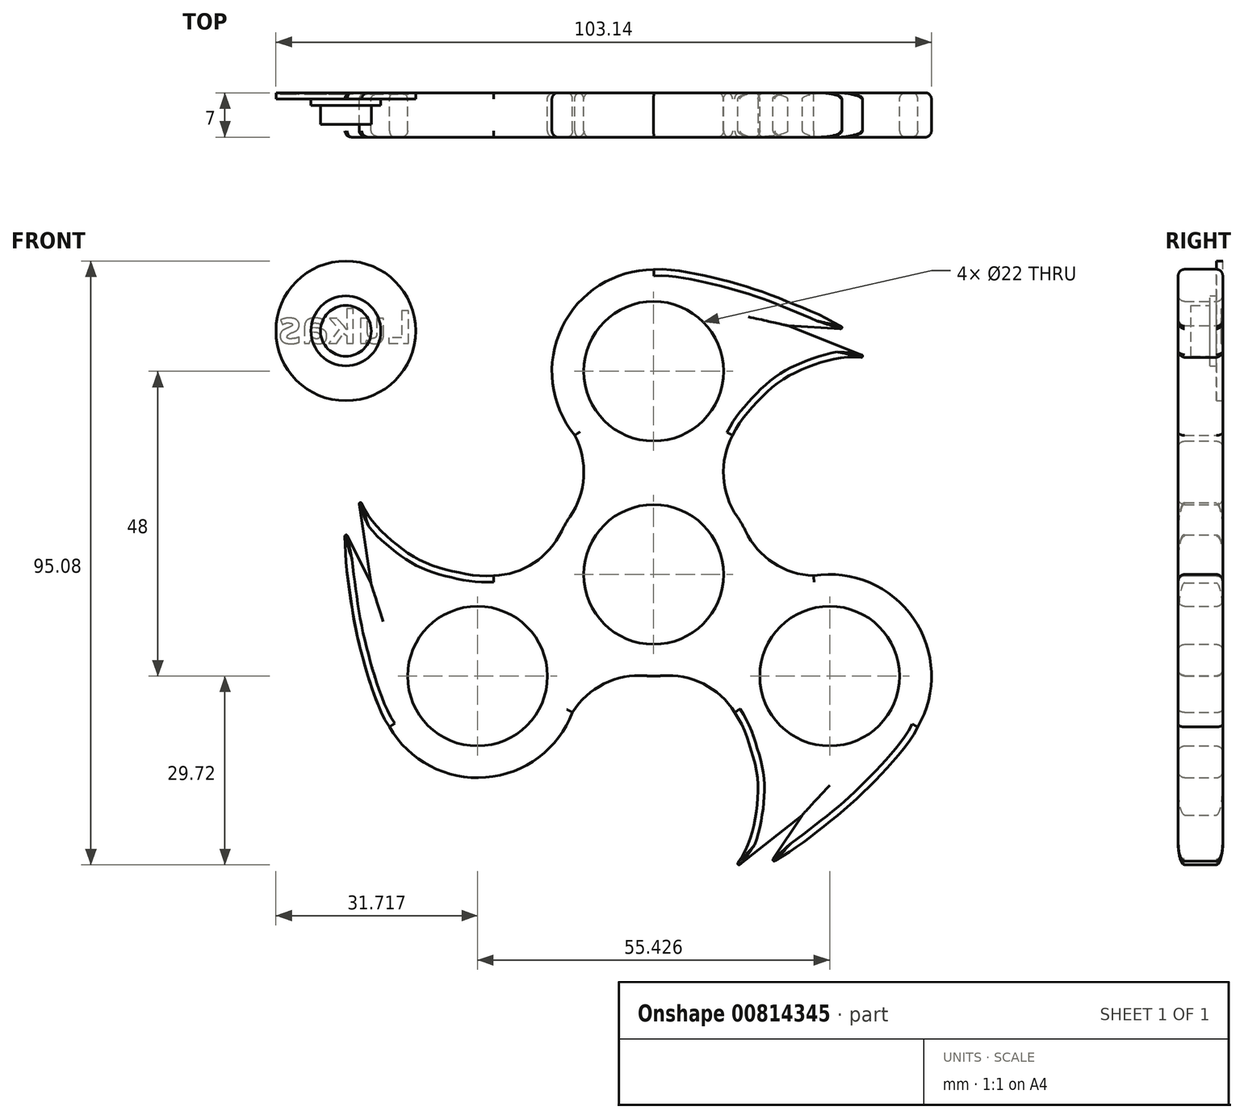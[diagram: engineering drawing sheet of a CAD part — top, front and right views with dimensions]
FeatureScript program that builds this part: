
annotation { "Feature Type Name" : "Feature", "Feature Type Description" : "" }
export const myFeature = defineFeature(function(context is Context, id is Id, definition is map)
    precondition{}
    {
        {
            var Q0;
            Q0=qCreatedBy(makeId("Front.planeOp"),FACE);
            var sketch = newSketch(context, id + "F0", { "sketchPlane" : qUnion([Q0])});
            skCircle(sketch, "E0", {"center": v(0, 0) * mm, "radius": 11 * mm});
            skArc(sketch, "E1", {"start": v(-13.17, 9.09) * mm, "mid": v(0, -16) * mm, "end": v(13.17, 9.09) * mm});
            skCircle(sketch, "E2", {"center": v(0, 32) * mm, "radius": 11 * mm});
            skLineSegment(sketch, "E3", {"start": v(12.42, 21.9) * mm, "end": v(12.42, 21.9) * mm});
            skFitSpline(sketch, "E4", {"points": [v(0, 48) * mm, v(15.63, 45) * mm, v(22.11, 42.54) * mm, v(30.28, 38.63) * mm], "startDerivative": vector(23.83, 2.95) * mm, "endDerivative": vector(45.32, -25.65) * mm});
            skLineSegment(sketch, "E5", {"start": v(30.28, 38.63) * mm, "end": v(21.1, 39.2) * mm});
            skLineSegment(sketch, "E6", {"start": v(21.1, 39.2) * mm, "end": v(34.96, 33.72) * mm});
            skFitSpline(sketch, "E7", {"points": [v(34.96, 33.72) * mm, v(23.56, 32.37) * mm, v(18.65, 29.47) * mm, v(15.85, 26.67) * mm, v(12.42, 21.9) * mm], "startDerivative": vector(-35.39, 11.82) * mm, "endDerivative": vector(-17.96, -33.28) * mm});
            skArc(sketch, "E8.trimOffspring", {"start": v(0, 48) * mm, "mid": v(-14.45, 38.88) * mm, "end": v(-12.42, 21.9) * mm});
            skArc(sketch, "E9", {"start": v(13.17, 9.09) * mm, "mid": v(11, 15.4) * mm, "end": v(12.42, 21.9) * mm});
            skArc(sketch, "E10.MirrorCS", {"start": v(-13.17, 9.09) * mm, "mid": v(-11, 15.4) * mm, "end": v(-12.42, 21.9) * mm});
            skSolve(sketch);
        }
        {
            var Q0;
            Q0=makeQuery(id+"F0.imprint","IMPRINT",FACE,{"disambiguationData":[TD([[makeQuery(id+"F0.imprint","IMPRINT",EDGE,{"derivedFrom":sQuery(id+"F0.wireOp",EDGE,"E0")}),-1.0]])]});
            extrude(context, id + "F1", {"entities" : qUnion([Q0]), "depth" : 7 * mm, "offsetDistance" : 25 * mm});
        }
        {
            var Q0;
            Q0=makeQuery(id+"F1.opExtrude","SWEPT_BODY",BODY,{"disambiguationData":[OSD([sQuery(id+"F0.wireOp",EDGE,"E0"),sQuery(id+"F0.wireOp",EDGE,"E1"),sQuery(id+"F0.wireOp",EDGE,"E2"),sQuery(id+"F0.wireOp",EDGE,"E3"),sQuery(id+"F0.wireOp",EDGE,"LkXJ2vyM-1mGQ-eDcK-5ijq-w6ZpazgIBIUJ"),sQuery(id+"F0.wireOp",EDGE,"5baaefb0-8613-44b4-96e0-c200b75026c80.MirrorCS"),sQuery(id+"F0.wireOp",EDGE,"E4"),sQuery(id+"F0.wireOp",EDGE,"E5"),sQuery(id+"F0.wireOp",EDGE,"E6"),sQuery(id+"F0.wireOp",EDGE,"E7"),sQuery(id+"F0.wireOp",EDGE,"E8.trimOffspring")])]});
            var Q1;
            Q1=makeQuery(id+"F1.opExtrude","SWEPT_FACE",FACE,{"disambiguationData":[OSD([sQuery(id+"F0.wireOp",EDGE,"E1")])]});
            circularPattern(context, id + "F2", {"entities" : qUnion([Q0]), "axis" : qUnion([Q1]), "angle" : 360 * degree, "instanceCount" : 3, "equalSpace" : true});
        }
        {
            var Q0;
            Q0=makeQuery(id+"F1.opExtrude","SWEPT_BODY",BODY,{"disambiguationData":[OSD([sQuery(id+"F0.wireOp",EDGE,"E0"),sQuery(id+"F0.wireOp",EDGE,"E1"),sQuery(id+"F0.wireOp",EDGE,"E2"),sQuery(id+"F0.wireOp",EDGE,"E3"),sQuery(id+"F0.wireOp",EDGE,"LkXJ2vyM-1mGQ-eDcK-5ijq-w6ZpazgIBIUJ"),sQuery(id+"F0.wireOp",EDGE,"5baaefb0-8613-44b4-96e0-c200b75026c80.MirrorCS"),sQuery(id+"F0.wireOp",EDGE,"E4"),sQuery(id+"F0.wireOp",EDGE,"E5"),sQuery(id+"F0.wireOp",EDGE,"E6"),sQuery(id+"F0.wireOp",EDGE,"E7"),sQuery(id+"F0.wireOp",EDGE,"E8.trimOffspring")])]});
            var Q1;
            Q1=makeQuery(id+"F2.opPattern","COPY",BODY,{"derivedFrom":makeQuery(id+"F1.opExtrude","SWEPT_BODY",BODY,{"disambiguationData":[OSD([sQuery(id+"F0.wireOp",EDGE,"E0"),sQuery(id+"F0.wireOp",EDGE,"E1"),sQuery(id+"F0.wireOp",EDGE,"E2"),sQuery(id+"F0.wireOp",EDGE,"E3"),sQuery(id+"F0.wireOp",EDGE,"LkXJ2vyM-1mGQ-eDcK-5ijq-w6ZpazgIBIUJ"),sQuery(id+"F0.wireOp",EDGE,"5baaefb0-8613-44b4-96e0-c200b75026c80.MirrorCS"),sQuery(id+"F0.wireOp",EDGE,"E4"),sQuery(id+"F0.wireOp",EDGE,"E5"),sQuery(id+"F0.wireOp",EDGE,"E6"),sQuery(id+"F0.wireOp",EDGE,"E7"),sQuery(id+"F0.wireOp",EDGE,"E8.trimOffspring")])]}),"instanceName":"1"});
            var Q2;
            Q2=makeQuery(id+"F2.opPattern","COPY",BODY,{"derivedFrom":makeQuery(id+"F1.opExtrude","SWEPT_BODY",BODY,{"disambiguationData":[OSD([sQuery(id+"F0.wireOp",EDGE,"E0"),sQuery(id+"F0.wireOp",EDGE,"E1"),sQuery(id+"F0.wireOp",EDGE,"E2"),sQuery(id+"F0.wireOp",EDGE,"E3"),sQuery(id+"F0.wireOp",EDGE,"LkXJ2vyM-1mGQ-eDcK-5ijq-w6ZpazgIBIUJ"),sQuery(id+"F0.wireOp",EDGE,"5baaefb0-8613-44b4-96e0-c200b75026c80.MirrorCS"),sQuery(id+"F0.wireOp",EDGE,"E4"),sQuery(id+"F0.wireOp",EDGE,"E5"),sQuery(id+"F0.wireOp",EDGE,"E6"),sQuery(id+"F0.wireOp",EDGE,"E7"),sQuery(id+"F0.wireOp",EDGE,"E8.trimOffspring")])]}),"instanceName":"2"});
            booleanBodies(context, id + "F3", {"operationType" : BooleanOperationType.UNION, "tools" : qUnion([Q0, Q1, Q2])});
        }
        {
            var Q0;
            {var subQ0=makeQuery(id+"F1.opExtrude","CAP_FACE",FACE,{"disambiguationData":[OSD([sQuery(id+"F0.wireOp",EDGE,"E0"),sQuery(id+"F0.wireOp",EDGE,"E1"),sQuery(id+"F0.wireOp",EDGE,"E2"),sQuery(id+"F0.wireOp",EDGE,"LkXJ2vyM-1mGQ-eDcK-5ijq-w6ZpazgIBIUJ"),sQuery(id+"F0.wireOp",EDGE,"5baaefb0-8613-44b4-96e0-c200b75026c80.MirrorCS"),sQuery(id+"F0.wireOp",EDGE,"E4"),sQuery(id+"F0.wireOp",EDGE,"E5"),sQuery(id+"F0.wireOp",EDGE,"E6"),sQuery(id+"F0.wireOp",EDGE,"E7"),sQuery(id+"F0.wireOp",EDGE,"E8.trimOffspring")])],"isStart":false});Q0=makeQuery(id+"F3.opBoolean","MERGE",FACE,{"derivedFrom":[subQ0,makeQuery(id+"F2.opPattern","COPY",FACE,{"derivedFrom":subQ0,"instanceName":"1"}),makeQuery(id+"F2.opPattern","COPY",FACE,{"derivedFrom":subQ0,"instanceName":"2"})]});}
            var Q1;
            {var subQ0=makeQuery(id+"F1.opExtrude","CAP_FACE",FACE,{"disambiguationData":[OSD([sQuery(id+"F0.wireOp",EDGE,"E0"),sQuery(id+"F0.wireOp",EDGE,"E1"),sQuery(id+"F0.wireOp",EDGE,"E2"),sQuery(id+"F0.wireOp",EDGE,"LkXJ2vyM-1mGQ-eDcK-5ijq-w6ZpazgIBIUJ"),sQuery(id+"F0.wireOp",EDGE,"5baaefb0-8613-44b4-96e0-c200b75026c80.MirrorCS"),sQuery(id+"F0.wireOp",EDGE,"E4"),sQuery(id+"F0.wireOp",EDGE,"E5"),sQuery(id+"F0.wireOp",EDGE,"E6"),sQuery(id+"F0.wireOp",EDGE,"E7"),sQuery(id+"F0.wireOp",EDGE,"E8.trimOffspring")])],"isStart":true});Q1=makeQuery(id+"F3.opBoolean","MERGE",FACE,{"derivedFrom":[subQ0,makeQuery(id+"F2.opPattern","COPY",FACE,{"derivedFrom":subQ0,"instanceName":"1"}),makeQuery(id+"F2.opPattern","COPY",FACE,{"derivedFrom":subQ0,"instanceName":"2"})]});}
            fillet(context, id + "F4", {"entities" : qUnion([Q0, Q1]), "radius" : 1 * mm, "tangentPropagation" : true, "allowEdgeOverflow" : false});
        }
        {
            var Q0;
            Q0=makeQuery(id+"F2.opPattern","COPY",EDGE,{"derivedFrom":makeQuery(id+"F1.opExtrude","SWEPT_EDGE",EDGE,{"disambiguationData":[OSD([sQuery(id+"F0.wireOp",EDGE,"E4"),sQuery(id+"F0.wireOp",EDGE,"E5")])]}),"instanceName":"2"});
            var Q1;
            Q1=makeQuery(id+"F2.opPattern","COPY",EDGE,{"derivedFrom":makeQuery(id+"F1.opExtrude","SWEPT_EDGE",EDGE,{"disambiguationData":[OSD([sQuery(id+"F0.wireOp",EDGE,"E6"),sQuery(id+"F0.wireOp",EDGE,"E7")])]}),"instanceName":"2"});
            var Q2;
            Q2=makeQuery(id+"F1.opExtrude","SWEPT_EDGE",EDGE,{"disambiguationData":[OSD([sQuery(id+"F0.wireOp",EDGE,"E6"),sQuery(id+"F0.wireOp",EDGE,"E7")])]});
            var Q3;
            Q3=makeQuery(id+"F1.opExtrude","SWEPT_EDGE",EDGE,{"disambiguationData":[OSD([sQuery(id+"F0.wireOp",EDGE,"E4"),sQuery(id+"F0.wireOp",EDGE,"E5")])]});
            var Q4;
            Q4=makeQuery(id+"F2.opPattern","COPY",EDGE,{"derivedFrom":makeQuery(id+"F1.opExtrude","SWEPT_EDGE",EDGE,{"disambiguationData":[OSD([sQuery(id+"F0.wireOp",EDGE,"E4"),sQuery(id+"F0.wireOp",EDGE,"E5")])]}),"instanceName":"1"});
            var Q5;
            Q5=makeQuery(id+"F2.opPattern","COPY",EDGE,{"derivedFrom":makeQuery(id+"F1.opExtrude","SWEPT_EDGE",EDGE,{"disambiguationData":[OSD([sQuery(id+"F0.wireOp",EDGE,"E6"),sQuery(id+"F0.wireOp",EDGE,"E7")])]}),"instanceName":"1"});
            fillet(context, id + "F5", {"entities" : qUnion([Q0, Q1, Q2, Q3, Q4, Q5]), "radius" : 0.2 * mm, "tangentPropagation" : true, "allowEdgeOverflow" : false});
        }
        {
            var Q0;
            Q0=qCreatedBy(makeId("Front.planeOp"),FACE);
            var sketch = newSketch(context, id + "F6", { "sketchPlane" : qUnion([Q0])});
            skCircle(sketch, "E11", {"center": v(-48.43, 38.36) * mm, "radius": 11 * mm});
            skCircle(sketch, "E12", {"center": v(-48.43, 38.36) * mm, "radius": 4 * mm});
            skCircle(sketch, "E13", {"center": v(-48.43, 38.36) * mm, "radius": 5.5 * mm});
            skSolve(sketch);
        }
        {
            var Q0;
            Q0=makeQuery(id+"F6.imprint","IMPRINT",FACE,{"disambiguationData":[TD([[makeQuery(id+"F6.imprint","IMPRINT",EDGE,{"derivedFrom":sQuery(id+"F6.wireOp",EDGE,"E11")}),1.0]])]});
            extrude(context, id + "F7", {"entities" : qUnion([Q0]), "depth" : 1 * mm, "offsetDistance" : 25 * mm});
        }
        {
            var Q0;
            Q0=makeQuery(id+"F6.imprint","IMPRINT",FACE,{"disambiguationData":[TD([[makeQuery(id+"F6.imprint","IMPRINT",EDGE,{"derivedFrom":sQuery(id+"F6.wireOp",EDGE,"E12")}),-1.0]])]});
            extrude(context, id + "F8", {"entities" : qUnion([Q0]), "operationType" : NewBodyOperationType.ADD, "depth" : 2 * mm, "offsetDistance" : 25 * mm});
        }
        {
            var Q0;
            Q0=makeQuery(id+"F6.imprint","IMPRINT",FACE,{"disambiguationData":[TD([[makeQuery(id+"F6.imprint","IMPRINT",EDGE,{"derivedFrom":sQuery(id+"F6.wireOp",EDGE,"E12")}),1.0]])]});
            extrude(context, id + "F9", {"entities" : qUnion([Q0]), "operationType" : NewBodyOperationType.ADD, "depth" : 5 * mm, "offsetDistance" : 25 * mm});
        }
        {
            var Q0;
            {var subQ0=sQuery(id+"F6.wireOp",EDGE,"E12");var subQ1=sQuery(id+"F6.wireOp",EDGE,"E13");Q0=makeQuery(id+"F9.boolean.opBoolean","MERGE",FACE,{"derivedFrom":[makeQuery(id+"F8.boolean.opBoolean","MERGE",FACE,{"derivedFrom":[makeQuery(id+"F7.opExtrude","CAP_FACE",FACE,{"disambiguationData":[OSD([sQuery(id+"F6.wireOp",EDGE,"E11"),subQ1])],"isStart":true}),makeQuery(id+"F8.opExtrude","CAP_FACE",FACE,{"disambiguationData":[OSD([subQ0,subQ1])],"isStart":true})]}),makeQuery(id+"F9.opExtrude","CAP_FACE",FACE,{"disambiguationData":[OSD([subQ0])],"isStart":true})]});}
            var sketch = newSketch(context, id + "F10", { "sketchPlane" : qUnion([Q0])});
            skText(sketch, "E14", { "text": "Lukas", "fontName": "OpenSans-Bold.ttf"});
            const initialGuessF10  = {"E14": [0.0379, 0.0364, 1, 0, 0.00517]};
            skSetInitialGuess(sketch, initialGuessF10);
            skSolve(sketch);
        }
        {
            var Q0;
            Q0 = qSketchRegion(id + "F10", true);
            extrude(context, id + "F11", {"entities" : qUnion([Q0]), "operationType" : NewBodyOperationType.REMOVE, "oppositeDirection" : true, "depth" : 0.2 * mm, "offsetDistance" : 25 * mm});
        }
    });
